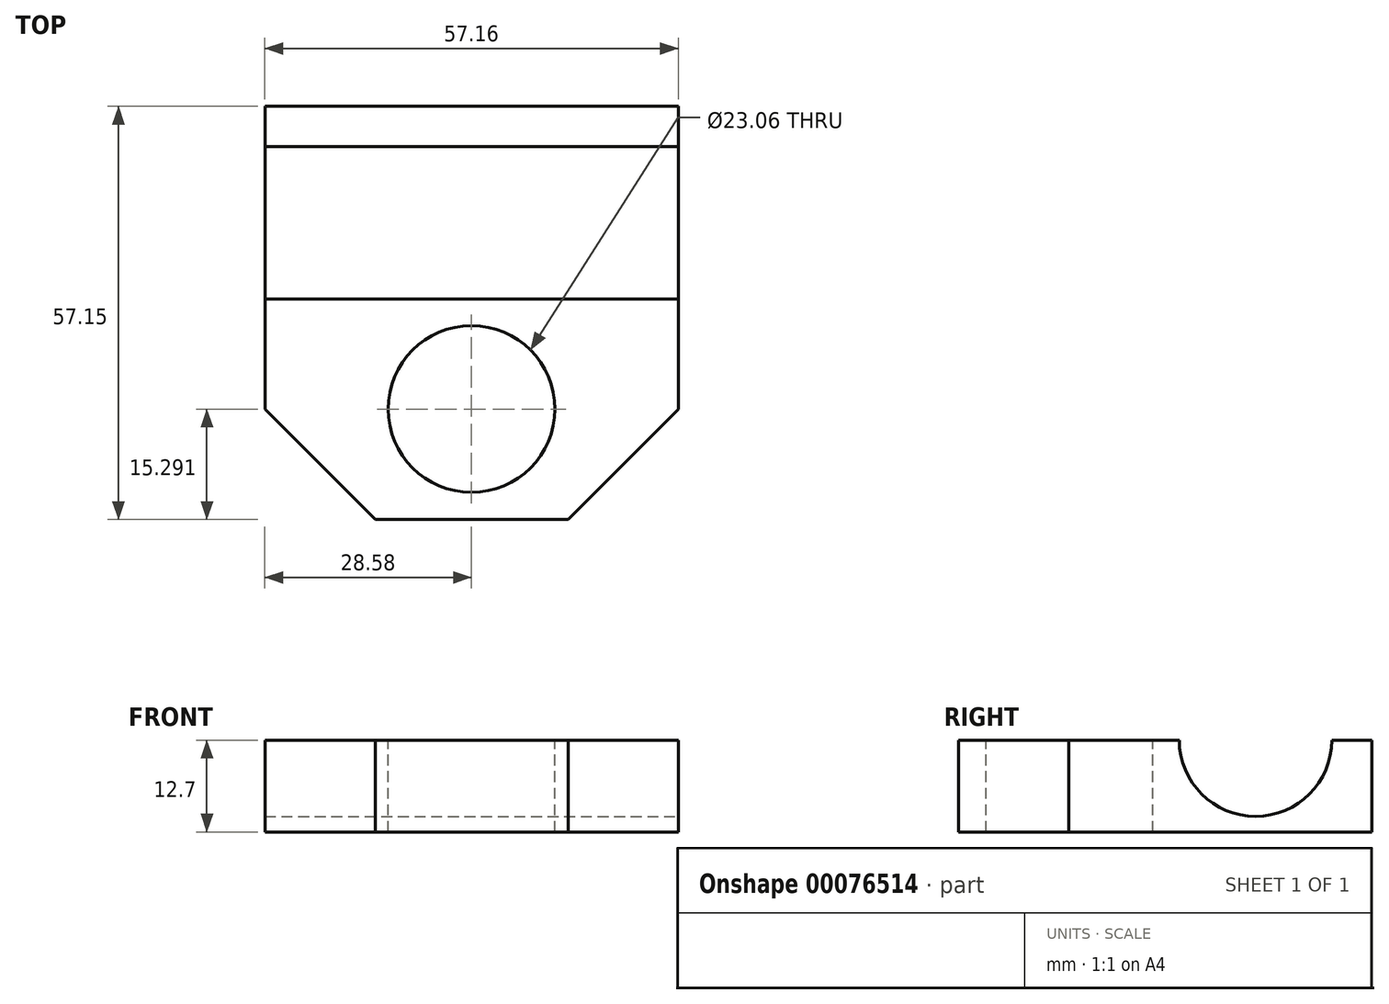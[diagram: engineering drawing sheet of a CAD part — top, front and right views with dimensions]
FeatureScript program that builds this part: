
annotation { "Feature Type Name" : "Feature", "Feature Type Description" : "" }
export const myFeature = defineFeature(function(context is Context, id is Id, definition is map)
    precondition{}
    {
        {
            var Q0;
            Q0=qCreatedBy(makeId("Top.planeOp"),FACE);
            var sketch = newSketch(context, id + "F0", { "sketchPlane" : qUnion([Q0])});
            skLineSegment(sketch, "E0", {"start": v(0, 28.58) * mm, "end": v(28.58, 28.58) * mm});
            skLineSegment(sketch, "E1", {"start": v(28.58, 28.58) * mm, "end": v(28.58, 0) * mm});
            skLineSegment(sketch, "E2.MirrorCS", {"start": v(0, -28.58) * mm, "end": v(28.58, -28.58) * mm});
            skLineSegment(sketch, "E3.MirrorCS", {"start": v(28.58, -28.58) * mm, "end": v(28.58, 0) * mm});
            skLineSegment(sketch, "E4.MirrorCS", {"start": v(0, -28.58) * mm, "end": v(-28.58, -28.58) * mm});
            skLineSegment(sketch, "E5.MirrorCS", {"start": v(-28.58, -28.58) * mm, "end": v(-28.58, 0) * mm});
            skLineSegment(sketch, "E6.MirrorCS", {"start": v(0, 28.58) * mm, "end": v(-28.58, 28.58) * mm});
            skLineSegment(sketch, "E7.MirrorCS", {"start": v(-28.58, 28.58) * mm, "end": v(-28.58, 0) * mm});
            skSolve(sketch);
        }
        {
            var Q0;
            Q0=makeQuery(id+"F0.imprint","IMPRINT",FACE,{"disambiguationData":[TD([[makeQuery(id+"F0.imprint","IMPRINT",EDGE,{"derivedFrom":sQuery(id+"F0.wireOp",EDGE,"E0")}),-1.0]])]});
            extrude(context, id + "F1", {"entities" : qUnion([Q0]), "depth" : 12.7 * mm});
        }
        {
            var Q0;
            Q0=makeQuery(id+"F1.opExtrude","SWEPT_EDGE",EDGE,{"disambiguationData":[OSD([sQuery(id+"F0.wireOp",EDGE,"E2.MirrorCS"),sQuery(id+"F0.wireOp",EDGE,"E3.MirrorCS")])]});
            var Q1;
            Q1=makeQuery(id+"F1.opExtrude","SWEPT_EDGE",EDGE,{"disambiguationData":[OSD([sQuery(id+"F0.wireOp",EDGE,"E4.MirrorCS"),sQuery(id+"F0.wireOp",EDGE,"E5.MirrorCS")])]});
            chamfer(context, id + "F2", {"entities" : qUnion([Q0, Q1]), "width" : 15.24 * mm, "tangentPropagation" : true});
        }
        {
            var Q0;
            Q0=makeQuery(id+"F1.opExtrude","CAP_FACE",FACE,{"disambiguationData":[OSD([sQuery(id+"F0.wireOp",EDGE,"E0"),sQuery(id+"F0.wireOp",EDGE,"E1"),sQuery(id+"F0.wireOp",EDGE,"E2.MirrorCS"),sQuery(id+"F0.wireOp",EDGE,"E3.MirrorCS"),sQuery(id+"F0.wireOp",EDGE,"E4.MirrorCS"),sQuery(id+"F0.wireOp",EDGE,"E5.MirrorCS"),sQuery(id+"F0.wireOp",EDGE,"E6.MirrorCS"),sQuery(id+"F0.wireOp",EDGE,"E7.MirrorCS")])],"isStart":false});
            var sketch = newSketch(context, id + "F3", { "sketchPlane" : qUnion([Q0])});
            skCircle(sketch, "E8", {"center": v(0, -13.29) * mm, "radius": 11.53 * mm});
            skSolve(sketch);
        }
        {
            var Q0;
            Q0=makeQuery(id+"F3.imprint","IMPRINT",FACE,{"disambiguationData":[TD([[makeQuery(id+"F3.imprint","IMPRINT",EDGE,{"derivedFrom":sQuery(id+"F3.wireOp",EDGE,"E8")}),1.0]])]});
            extrude(context, id + "F4", {"entities" : qUnion([Q0]), "operationType" : NewBodyOperationType.REMOVE, "oppositeDirection" : true, "depth" : 12.7 * mm});
        }
        {
            var Q0;
            Q0=makeQuery(id+"F1.opExtrude","SWEPT_FACE",FACE,{"disambiguationData":[OSD([sQuery(id+"F0.wireOp",EDGE,"E1"),sQuery(id+"F0.wireOp",EDGE,"E3.MirrorCS")])]});
            var sketch = newSketch(context, id + "F5", { "sketchPlane" : qUnion([Q0])});
            skArc(sketch, "E9", {"start": v(1.92, 12.7) * mm, "mid": v(12.47, 2.16) * mm, "end": v(23.01, 12.7) * mm});
            skSolve(sketch);
        }
        {
            var Q0;
            {var subQ0=sQuery(id+"F5.wireOp",EDGE,"E9");Q0=makeQuery(id+"F5.imprint","IMPRINT",FACE,{"disambiguationData":[TD([[makeQuery(id+"F5.imprint","IMPRINT",EDGE,{"derivedFrom":subQ0}),1.0]])]});}
            extrude(context, id + "F6", {"entities" : qUnion([Q0]), "operationType" : NewBodyOperationType.REMOVE, "oppositeDirection" : true, "depth" : 63.5 * mm});
        }
    });
